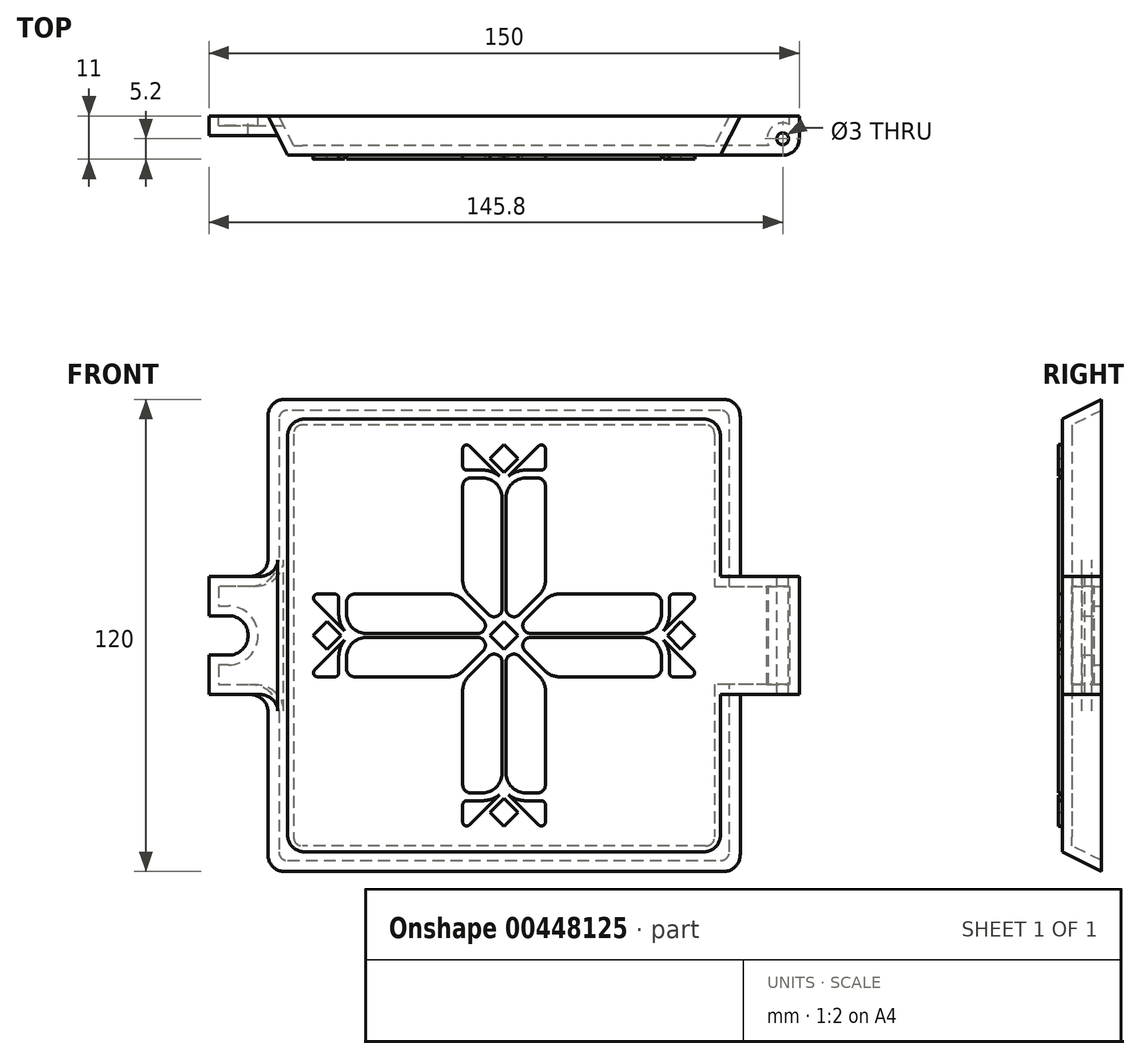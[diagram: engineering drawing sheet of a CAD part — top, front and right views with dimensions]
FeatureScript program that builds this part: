
annotation { "Feature Type Name" : "Feature", "Feature Type Description" : "" }
export const myFeature = defineFeature(function(context is Context, id is Id, definition is map)
    precondition{}
    {
        {
            var Q0;
            Q0=qCreatedBy(makeId("Front.planeOp"),FACE);
            var sketch = newSketch(context, id + "F0", { "sketchPlane" : qUnion([Q0])});
            skLineSegment(sketch, "E0.bottom", {"start": v(60, 60) * mm, "end": v(-60, 60) * mm});
            skLineSegment(sketch, "E0.top", {"start": v(60, -60) * mm, "end": v(-60, -60) * mm});
            skLineSegment(sketch, "E0.left", {"start": v(60, 60) * mm, "end": v(60, -60) * mm});
            skLineSegment(sketch, "E0.right", {"start": v(-60, 60) * mm, "end": v(-60, -60) * mm});
            skPoint(sketch, "E0.middle", {"position": v(0, 0) * mm});
            skLineSegment(sketch, "E1", {"start": v(60, 15) * mm, "end": v(75, 15) * mm});
            skLineSegment(sketch, "E2", {"start": v(75, 15) * mm, "end": v(75, -15) * mm});
            skLineSegment(sketch, "E3", {"start": v(75, -15) * mm, "end": v(60, -15) * mm});
            skLineSegment(sketch, "E4", {"start": v(-60, 15) * mm, "end": v(-75, 15) * mm});
            skLineSegment(sketch, "E5", {"start": v(-75, 15) * mm, "end": v(-75, 5) * mm});
            skLineSegment(sketch, "E6", {"start": v(-75, 5) * mm, "end": v(-70, 5) * mm});
            skLineSegment(sketch, "E7", {"start": v(-65, 0) * mm, "end": v(-65, 0) * mm});
            skLineSegment(sketch, "E8", {"start": v(-70, -5) * mm, "end": v(-75, -5) * mm});
            skLineSegment(sketch, "E9", {"start": v(-75, -5) * mm, "end": v(-75, -15) * mm});
            skLineSegment(sketch, "E10", {"start": v(-75, -15) * mm, "end": v(-60, -15) * mm});
            skPoint(sketch, "E11.visualSharp", {"position": v(-65, 5) * mm});
            skArc(sketch, "E11.filletArc", {"start": v(-65, 0) * mm, "mid": v(-66.46, 3.54) * mm, "end": v(-70, 5) * mm});
            skPoint(sketch, "E12.visualSharp", {"position": v(-65, -5) * mm});
            skArc(sketch, "E12.filletArc", {"start": v(-70, -5) * mm, "mid": v(-66.46, -3.54) * mm, "end": v(-65, 0) * mm});
            skSolve(sketch);
        }
        {
            var Q0;
            {var subQ3=sQuery(id+"F0.wireOp",EDGE,"E0.bottom");Q0=makeQuery(id+"F0.imprint","IMPRINT",FACE,{"disambiguationData":[TD([[makeQuery(id+"F0.imprint","IMPRINT",EDGE,{"derivedFrom":subQ3}),1.0]])]});}
            var Q1;
            {var subQ0=sQuery(id+"F0.wireOp",EDGE,"E1");Q1=makeQuery(id+"F0.imprint","IMPRINT",FACE,{"disambiguationData":[TD([[makeQuery(id+"F0.imprint","IMPRINT",EDGE,{"derivedFrom":subQ0}),-1.0]])]});}
            extrude(context, id + "F1", {"entities" : qUnion([Q0, Q1]), "depth" : 10 * mm});
        }
        {
            var Q0;
            {var subQ0=sQuery(id+"F0.wireOp",EDGE,"E4");Q0=makeQuery(id+"F0.imprint","IMPRINT",FACE,{"disambiguationData":[TD([[makeQuery(id+"F0.imprint","IMPRINT",EDGE,{"derivedFrom":subQ0}),1.0]])]});}
            extrude(context, id + "F2", {"entities" : qUnion([Q0]), "operationType" : NewBodyOperationType.ADD, "depth" : 5 * mm});
        }
        {
            var Q0;
            Q0=makeQuery(id+"F1.opExtrude","CAP_EDGE",EDGE,{"disambiguationData":[OSD([sQuery(id+"F0.wireOp",EDGE,"E0.bottom")])],"isStart":false});
            var Q1;
            {var subQ0=sQuery(id+"F0.wireOp",EDGE,"E0.left");Q1=makeQuery(id+"F1.opExtrude","CAP_EDGE",EDGE,{"disambiguationData":[OSD([subQ0]),TDD([makeQuery(id+"F0.imprint","IMPRINT",EDGE,{"disambiguationData":[TD([[makeQuery(id+"F0.imprint","INTERSECT",VERTEX,{"derivedFrom":[sQuery(id+"F0.wireOp",EDGE,"E0.bottom"),subQ0]}),-1.0]])],"derivedFrom":subQ0})])],"isStart":false});}
            var Q2;
            {var subQ0=sQuery(id+"F0.wireOp",EDGE,"E0.left");Q2=makeQuery(id+"F1.opExtrude","CAP_EDGE",EDGE,{"disambiguationData":[OSD([subQ0]),TDD([makeQuery(id+"F0.imprint","IMPRINT",EDGE,{"disambiguationData":[TD([[makeQuery(id+"F0.imprint","INTERSECT",VERTEX,{"derivedFrom":[sQuery(id+"F0.wireOp",EDGE,"E0.top"),subQ0]}),1.0]])],"derivedFrom":subQ0})])],"isStart":false});}
            var Q3;
            Q3=makeQuery(id+"F1.opExtrude","CAP_EDGE",EDGE,{"disambiguationData":[OSD([sQuery(id+"F0.wireOp",EDGE,"E0.top")])],"isStart":false});
            var Q4;
            Q4=makeQuery(id+"F1.opExtrude","CAP_EDGE",EDGE,{"disambiguationData":[OSD([sQuery(id+"F0.wireOp",EDGE,"E0.right")])],"isStart":false});
            chamfer(context, id + "F3", {"entities" : qUnion([Q0, Q1, Q2, Q3, Q4]), "chamferType" : ChamferType.TWO_OFFSETS, "width1" : 5 * mm, "oppositeDirection" : false, "width2" : 10 * mm, "tangentPropagation" : true});
        }
        {
            var Q0;
            Q0=makeQuery(id+"F1.opExtrude","CAP_EDGE",EDGE,{"disambiguationData":[OSD([sQuery(id+"F0.wireOp",EDGE,"E2")])],"isStart":false});
            var Q1;
            Q1=makeQuery(id+"F3.opChamfer","BLEND_EDGE",EDGE,{"blendedFrom":[makeQuery(id+"F1.opExtrude","CAP_EDGE",EDGE,{"disambiguationData":[OSD([sQuery(id+"F0.wireOp",EDGE,"E0.right")])],"isStart":false}),makeQuery(id+"F2.opExtrude","SWEPT_FACE",FACE,{"disambiguationData":[OSD([sQuery(id+"F0.wireOp",EDGE,"E4")])]})],"blendedInto":[makeQuery(id+"F2.opExtrude","SWEPT_FACE",FACE,{"disambiguationData":[OSD([sQuery(id+"F0.wireOp",EDGE,"E4")])]})]});
            var Q2;
            Q2=makeQuery(id+"F3.opChamfer","BLEND_EDGE",EDGE,{"blendedFrom":[makeQuery(id+"F1.opExtrude","CAP_EDGE",EDGE,{"disambiguationData":[OSD([sQuery(id+"F0.wireOp",EDGE,"E0.right")])],"isStart":false}),makeQuery(id+"F2.opExtrude","SWEPT_FACE",FACE,{"disambiguationData":[OSD([sQuery(id+"F0.wireOp",EDGE,"E10")])]})],"blendedInto":[makeQuery(id+"F2.opExtrude","SWEPT_FACE",FACE,{"disambiguationData":[OSD([sQuery(id+"F0.wireOp",EDGE,"E10")])]})]});
            fillet(context, id + "F4", {"entities" : qUnion([Q0, Q1, Q2]), "radius" : 4.2 * mm, "tangentPropagation" : true, "allowEdgeOverflow" : false});
        }
        {
            var Q0;
            Q0=makeQuery(id+"F1.opExtrude","SWEPT_FACE",FACE,{"disambiguationData":[OSD([sQuery(id+"F0.wireOp",EDGE,"E1")])]});
            var sketch = newSketch(context, id + "F5", { "sketchPlane" : qUnion([Q0])});
            skPoint(sketch, "E13", {"position": v(70.8, -5.8) * mm});
            skSolve(sketch);
        }
        {
            var Q0;
            Q0=sQuery(id+"F5.wireOp",VERTEX,"E13");
            var Q1;
            Q1=makeQuery(id+"F1.opExtrude","SWEPT_BODY",BODY,{"disambiguationData":[OSD([sQuery(id+"F0.wireOp",EDGE,"E0.bottom"),sQuery(id+"F0.wireOp",EDGE,"E0.top"),sQuery(id+"F0.wireOp",EDGE,"E0.left"),sQuery(id+"F0.wireOp",EDGE,"E0.right"),sQuery(id+"F0.wireOp",EDGE,"E1"),sQuery(id+"F0.wireOp",EDGE,"E2"),sQuery(id+"F0.wireOp",EDGE,"E3")])]});
            hole(context, id + "F6", {"style" : HoleStyle.SIMPLE, "endStyle" : HoleEndStyle.THROUGH, "holeDiameter" : 3 * mm, "isTappedThrough" : true, "tappedDepth" : 12 * mm, "tapClearance" : 3, "locations" : qUnion([Q0]), "scope" : qUnion([Q1])});
        }
        {
            var Q0;
            {var subQ0=sQuery(id+"F0.wireOp",EDGE,"E0.left");var subQ1=sQuery(id+"F0.wireOp",EDGE,"E0.bottom");Q0=makeQuery(id+"F3.opChamfer","BLEND_EDGE",EDGE,{"blendedFrom":[makeQuery(id+"F1.opExtrude","CAP_EDGE",EDGE,{"disambiguationData":[OSD([subQ1])],"isStart":false}),makeQuery(id+"F1.opExtrude","CAP_EDGE",EDGE,{"disambiguationData":[OSD([subQ0]),TDD([makeQuery(id+"F0.imprint","IMPRINT",EDGE,{"disambiguationData":[TD([[makeQuery(id+"F0.imprint","INTERSECT",VERTEX,{"derivedFrom":[subQ1,subQ0]}),-1.0]])],"derivedFrom":subQ0})])],"isStart":false})],"blendedInto":[]});}
            var Q1;
            {var subQ0=sQuery(id+"F0.wireOp",EDGE,"E0.left");var subQ1=sQuery(id+"F0.wireOp",EDGE,"E0.top");Q1=makeQuery(id+"F3.opChamfer","BLEND_EDGE",EDGE,{"blendedFrom":[makeQuery(id+"F1.opExtrude","CAP_EDGE",EDGE,{"disambiguationData":[OSD([subQ1])],"isStart":false}),makeQuery(id+"F1.opExtrude","CAP_EDGE",EDGE,{"disambiguationData":[OSD([subQ0]),TDD([makeQuery(id+"F0.imprint","IMPRINT",EDGE,{"disambiguationData":[TD([[makeQuery(id+"F0.imprint","INTERSECT",VERTEX,{"derivedFrom":[subQ1,subQ0]}),1.0]])],"derivedFrom":subQ0})])],"isStart":false})],"blendedInto":[]});}
            var Q2;
            Q2=makeQuery(id+"F3.opChamfer","BLEND_EDGE",EDGE,{"blendedFrom":[makeQuery(id+"F1.opExtrude","CAP_EDGE",EDGE,{"disambiguationData":[OSD([sQuery(id+"F0.wireOp",EDGE,"E0.bottom")])],"isStart":false}),makeQuery(id+"F1.opExtrude","CAP_EDGE",EDGE,{"disambiguationData":[OSD([sQuery(id+"F0.wireOp",EDGE,"E0.right")])],"isStart":false})],"blendedInto":[]});
            var Q3;
            Q3=makeQuery(id+"F3.opChamfer","BLEND_EDGE",EDGE,{"blendedFrom":[makeQuery(id+"F1.opExtrude","CAP_EDGE",EDGE,{"disambiguationData":[OSD([sQuery(id+"F0.wireOp",EDGE,"E0.top")])],"isStart":false}),makeQuery(id+"F1.opExtrude","CAP_EDGE",EDGE,{"disambiguationData":[OSD([sQuery(id+"F0.wireOp",EDGE,"E0.right")])],"isStart":false})],"blendedInto":[]});
            fillet(context, id + "F7", {"entities" : qUnion([Q0, Q1, Q2, Q3]), "radius" : 5 * mm, "tangentPropagation" : true, "allowEdgeOverflow" : false});
        }
        {
            var Q0;
            {var subQ0=sQuery(id+"F0.wireOp",EDGE,"E0.right");Q0=makeQuery(id+"F2.boolean.opBoolean","MERGE",FACE,{"derivedFrom":[makeQuery(id+"F1.opExtrude","CAP_FACE",FACE,{"disambiguationData":[OSD([sQuery(id+"F0.wireOp",EDGE,"E0.bottom"),sQuery(id+"F0.wireOp",EDGE,"E0.top"),sQuery(id+"F0.wireOp",EDGE,"E0.left"),subQ0,sQuery(id+"F0.wireOp",EDGE,"E1"),sQuery(id+"F0.wireOp",EDGE,"E2"),sQuery(id+"F0.wireOp",EDGE,"E3")])],"isStart":true}),makeQuery(id+"F2.opExtrude","CAP_FACE",FACE,{"disambiguationData":[OSD([subQ0,sQuery(id+"F0.wireOp",EDGE,"E4"),sQuery(id+"F0.wireOp",EDGE,"E5"),sQuery(id+"F0.wireOp",EDGE,"E6"),sQuery(id+"F0.wireOp",EDGE,"E8"),sQuery(id+"F0.wireOp",EDGE,"E9"),sQuery(id+"F0.wireOp",EDGE,"E10"),sQuery(id+"F0.wireOp",EDGE,"E11.filletArc"),sQuery(id+"F0.wireOp",EDGE,"E12.filletArc")])],"isStart":true})]});}
            shell(context, id + "F8", {"entities" : qUnion([Q0]), "thickness" : 2.5 * mm});
        }
        {
            var Q0;
            Q0=makeQuery(id+"F1.opExtrude","CAP_FACE",FACE,{"disambiguationData":[OSD([sQuery(id+"F0.wireOp",EDGE,"E0.bottom"),sQuery(id+"F0.wireOp",EDGE,"E0.top"),sQuery(id+"F0.wireOp",EDGE,"E0.left"),sQuery(id+"F0.wireOp",EDGE,"E0.right"),sQuery(id+"F0.wireOp",EDGE,"E1"),sQuery(id+"F0.wireOp",EDGE,"E2"),sQuery(id+"F0.wireOp",EDGE,"E3")])],"isStart":false});
            var sketch = newSketch(context, id + "F9", { "sketchPlane" : qUnion([Q0])});
            skLineSegment(sketch, "E14.bottom", {"start": v(55, 55) * mm, "end": v(-55, 55) * mm, "construction": true});
            skLineSegment(sketch, "E14.top", {"start": v(55, -55) * mm, "end": v(-55, -55) * mm, "construction": true});
            skLineSegment(sketch, "E14.left", {"start": v(55, 55) * mm, "end": v(55, -55) * mm, "construction": true});
            skLineSegment(sketch, "E14.right", {"start": v(-55, 55) * mm, "end": v(-55, -55) * mm, "construction": true});
            skPoint(sketch, "E14.middle", {"position": v(0, 0) * mm});
            skPoint(sketch, "E14.middle.positionSnap0", {"position": v(-55, 0) * mm});
            skPoint(sketch, "E14.middle.positionSnap1", {"position": v(0, 55) * mm});
            skPoint(sketch, "E14.centerSnap0", {"position": v(-55, 0) * mm});
            skPoint(sketch, "E14.centerSnap1", {"position": v(0, 55) * mm});
            skLineSegment(sketch, "E15", {"start": v(-55, 0) * mm, "end": v(55, 0) * mm, "construction": true});
            skLineSegment(sketch, "E16", {"start": v(0, 55) * mm, "end": v(0, -55) * mm, "construction": true});
            skLineSegment(sketch, "E17", {"start": v(-55, -55) * mm, "end": v(55, 55) * mm, "construction": true});
            skLineSegment(sketch, "E18", {"start": v(-55, 55) * mm, "end": v(55, -55) * mm, "construction": true});
            skLineSegment(sketch, "E19", {"start": v(0, 3.54) * mm, "end": v(3.54, 0) * mm});
            skLineSegment(sketch, "E20", {"start": v(3.54, 0) * mm, "end": v(0, -3.54) * mm});
            skLineSegment(sketch, "E21", {"start": v(0, -3.54) * mm, "end": v(-3.54, 0) * mm});
            skLineSegment(sketch, "E22", {"start": v(-3.54, 0) * mm, "end": v(0, 3.54) * mm});
            skLineSegment(sketch, "E23.1.0.0", {"start": v(45, 3.54) * mm, "end": v(48.54, 0) * mm});
            skLineSegment(sketch, "E23.1.0.1", {"start": v(48.54, 0) * mm, "end": v(45, -3.54) * mm});
            skLineSegment(sketch, "E23.1.0.2", {"start": v(45, -3.54) * mm, "end": v(41.46, 0) * mm});
            skLineSegment(sketch, "E23.1.0.3", {"start": v(41.46, 0) * mm, "end": v(45, 3.54) * mm});
            skLineSegment(sketch, "E23.direction1", {"start": v(3.54, 0) * mm, "end": v(48.54, 0) * mm, "construction": true});
            skLineSegment(sketch, "E24", {"start": v(5.33, 3.91) * mm, "end": v(10.45, 9.04) * mm});
            skLineSegment(sketch, "E25", {"start": v(6.74, 0.5) * mm, "end": v(35, 0.5) * mm});
            skLineSegment(sketch, "E26", {"start": v(39.33, 0) * mm, "end": v(48.12, 8.8) * mm});
            skLineSegment(sketch, "E27", {"start": v(38, 10.5) * mm, "end": v(13.99, 10.5) * mm});
            skLineSegment(sketch, "E28", {"start": v(40, 5.5) * mm, "end": v(40, 8.5) * mm});
            skPoint(sketch, "E29.visualSharp", {"position": v(1.91, 0.5) * mm});
            skArc(sketch, "E29.filletArc", {"start": v(5.33, 3.91) * mm, "mid": v(4.9, 1.73) * mm, "end": v(6.74, 0.5) * mm});
            skPoint(sketch, "E30.visualSharp", {"position": v(11.91, 10.5) * mm});
            skArc(sketch, "E30.filletArc", {"start": v(13.99, 10.5) * mm, "mid": v(12.07, 10.12) * mm, "end": v(10.45, 9.04) * mm});
            skArc(sketch, "E31.filletArc", {"start": v(35, 0.5) * mm, "mid": v(38.54, 1.96) * mm, "end": v(40, 5.5) * mm});
            skArc(sketch, "E32.filletArc", {"start": v(40, 8.5) * mm, "mid": v(39.41, 9.91) * mm, "end": v(38, 10.5) * mm});
            skArc(sketch, "E33.0", {"start": v(39.33, 0) * mm, "mid": v(41.3, 2.44) * mm, "end": v(42, 5.5) * mm});
            skLineSegment(sketch, "E34", {"start": v(42, 5.5) * mm, "end": v(42, 9.5) * mm});
            skLineSegment(sketch, "E35", {"start": v(43, 10.5) * mm, "end": v(47.42, 10.5) * mm});
            skPoint(sketch, "E36.visualSharp", {"position": v(42, 10.5) * mm});
            skArc(sketch, "E36.filletArc", {"start": v(43, 10.5) * mm, "mid": v(42.3, 10.2) * mm, "end": v(42, 9.5) * mm});
            skPoint(sketch, "E37.visualSharp", {"position": v(49.83, 10.5) * mm});
            skArc(sketch, "E37.filletArc", {"start": v(48.12, 8.8) * mm, "mid": v(48.34, 9.88) * mm, "end": v(47.42, 10.5) * mm});
            skLineSegment(sketch, "E38", {"start": v(41.46, 0) * mm, "end": v(48.54, 0) * mm});
            skLineSegment(sketch, "E39.MirrorCS", {"start": v(6.74, -0.5) * mm, "end": v(35, -0.5) * mm});
            skArc(sketch, "E40.MirrorCS", {"start": v(5.33, -3.91) * mm, "mid": v(4.9, -1.73) * mm, "end": v(6.74, -0.5) * mm});
            skLineSegment(sketch, "E41.MirrorCS", {"start": v(5.33, -3.91) * mm, "end": v(10.45, -9.04) * mm});
            skPoint(sketch, "E42.MirrorP", {"position": v(11.91, -10.5) * mm});
            skLineSegment(sketch, "E43.MirrorCS", {"start": v(38, -10.5) * mm, "end": v(13.99, -10.5) * mm});
            skArc(sketch, "E44.MirrorCS", {"start": v(13.99, -10.5) * mm, "mid": v(12.07, -10.12) * mm, "end": v(10.45, -9.04) * mm});
            skArc(sketch, "E45.MirrorCS", {"start": v(40, -8.5) * mm, "mid": v(39.41, -9.91) * mm, "end": v(38, -10.5) * mm});
            skLineSegment(sketch, "E46.MirrorCS", {"start": v(40, -5.5) * mm, "end": v(40, -8.5) * mm});
            skArc(sketch, "E47.MirrorCS", {"start": v(35, -0.5) * mm, "mid": v(38.54, -1.96) * mm, "end": v(40, -5.5) * mm});
            skLineSegment(sketch, "E48.MirrorCS", {"start": v(39.33, 0) * mm, "end": v(48.12, -8.8) * mm});
            skLineSegment(sketch, "E49.MirrorCS", {"start": v(43, -10.5) * mm, "end": v(47.42, -10.5) * mm});
            skArc(sketch, "E50.MirrorCS", {"start": v(48.12, -8.8) * mm, "mid": v(48.34, -9.88) * mm, "end": v(47.42, -10.5) * mm});
            skArc(sketch, "E51.MirrorCS", {"start": v(43, -10.5) * mm, "mid": v(42.3, -10.2) * mm, "end": v(42, -9.5) * mm});
            skLineSegment(sketch, "E52.MirrorCS", {"start": v(42, -5.5) * mm, "end": v(42, -9.5) * mm});
            skArc(sketch, "E53.MirrorCS", {"start": v(39.33, 0) * mm, "mid": v(41.3, -2.44) * mm, "end": v(42, -5.5) * mm});
            skLineSegment(sketch, "E54.1.0", {"start": v(-0.5, -6.74) * mm, "end": v(-0.5, -35) * mm});
            skArc(sketch, "E54.1.1", {"start": v(-0.5, -35) * mm, "mid": v(-1.96, -38.54) * mm, "end": v(-5.5, -40) * mm});
            skLineSegment(sketch, "E54.1.2", {"start": v(-3.54, -45) * mm, "end": v(0, -41.46) * mm});
            skLineSegment(sketch, "E54.1.3", {"start": v(0, -41.46) * mm, "end": v(3.54, -45) * mm});
            skArc(sketch, "E54.1.5", {"start": v(3.91, -5.33) * mm, "mid": v(1.73, -4.9) * mm, "end": v(0.5, -6.74) * mm});
            skLineSegment(sketch, "E54.1.6", {"start": v(-5.5, -42) * mm, "end": v(-9.5, -42) * mm});
            skLineSegment(sketch, "E54.1.7", {"start": v(5.5, -42) * mm, "end": v(9.5, -42) * mm});
            skPoint(sketch, "E54.1.8", {"position": v(10.5, -42) * mm});
            skLineSegment(sketch, "E54.1.9", {"start": v(10.5, -38) * mm, "end": v(10.5, -13.99) * mm});
            skArc(sketch, "E54.1.10", {"start": v(0, -39.33) * mm, "mid": v(-2.44, -41.3) * mm, "end": v(-5.5, -42) * mm});
            skPoint(sketch, "E54.1.11", {"position": v(-10.5, -11.91) * mm});
            skLineSegment(sketch, "E54.1.12", {"start": v(3.91, -5.33) * mm, "end": v(9.04, -10.45) * mm});
            skLineSegment(sketch, "E54.1.13", {"start": v(3.54, -45) * mm, "end": v(0, -48.54) * mm});
            skLineSegment(sketch, "E54.1.14", {"start": v(0, -39.33) * mm, "end": v(8.8, -48.12) * mm});
            skLineSegment(sketch, "E54.1.15", {"start": v(-3.91, -5.33) * mm, "end": v(-9.04, -10.45) * mm});
            skPoint(sketch, "E54.1.16", {"position": v(10.5, -11.91) * mm});
            skLineSegment(sketch, "E54.1.17", {"start": v(0.5, -6.74) * mm, "end": v(0.5, -35) * mm});
            skArc(sketch, "E54.1.18", {"start": v(0.5, -35) * mm, "mid": v(1.96, -38.54) * mm, "end": v(5.5, -40) * mm});
            skLineSegment(sketch, "E54.1.19", {"start": v(0, -48.54) * mm, "end": v(-3.54, -45) * mm});
            skLineSegment(sketch, "E54.1.20", {"start": v(0, -39.33) * mm, "end": v(-8.8, -48.12) * mm});
            skArc(sketch, "E54.1.21", {"start": v(0, -39.33) * mm, "mid": v(2.44, -41.3) * mm, "end": v(5.5, -42) * mm});
            skLineSegment(sketch, "E54.1.22", {"start": v(-10.5, -38) * mm, "end": v(-10.5, -13.99) * mm});
            skArc(sketch, "E54.1.23", {"start": v(-3.91, -5.33) * mm, "mid": v(-1.73, -4.9) * mm, "end": v(-0.5, -6.74) * mm});
            skPoint(sketch, "E54.1.24", {"position": v(10.5, -49.83) * mm});
            skLineSegment(sketch, "E54.1.25", {"start": v(-10.5, -43) * mm, "end": v(-10.5, -47.42) * mm});
            skLineSegment(sketch, "E54.1.26", {"start": v(10.5, -43) * mm, "end": v(10.5, -47.42) * mm});
            skLineSegment(sketch, "E54.1.27", {"start": v(0, -41.46) * mm, "end": v(0, -48.54) * mm});
            skArc(sketch, "E54.1.28", {"start": v(10.5, -13.99) * mm, "mid": v(10.12, -12.07) * mm, "end": v(9.04, -10.45) * mm});
            skArc(sketch, "E54.1.29", {"start": v(-10.5, -13.99) * mm, "mid": v(-10.12, -12.07) * mm, "end": v(-9.04, -10.45) * mm});
            skLineSegment(sketch, "E54.1.30", {"start": v(5.5, -40) * mm, "end": v(8.5, -40) * mm});
            skLineSegment(sketch, "E54.1.31", {"start": v(-5.5, -40) * mm, "end": v(-8.5, -40) * mm});
            skArc(sketch, "E54.1.32", {"start": v(8.8, -48.12) * mm, "mid": v(9.88, -48.34) * mm, "end": v(10.5, -47.42) * mm});
            skArc(sketch, "E54.1.33", {"start": v(-8.5, -40) * mm, "mid": v(-9.91, -39.41) * mm, "end": v(-10.5, -38) * mm});
            skArc(sketch, "E54.1.34", {"start": v(10.5, -43) * mm, "mid": v(10.2, -42.3) * mm, "end": v(9.5, -42) * mm});
            skArc(sketch, "E54.1.35", {"start": v(-10.5, -43) * mm, "mid": v(-10.2, -42.3) * mm, "end": v(-9.5, -42) * mm});
            skArc(sketch, "E54.1.36", {"start": v(-8.8, -48.12) * mm, "mid": v(-9.88, -48.34) * mm, "end": v(-10.5, -47.42) * mm});
            skArc(sketch, "E54.1.37", {"start": v(8.5, -40) * mm, "mid": v(9.91, -39.41) * mm, "end": v(10.5, -38) * mm});
            skLineSegment(sketch, "E54.2.0", {"start": v(-6.74, 0.5) * mm, "end": v(-35, 0.5) * mm});
            skArc(sketch, "E54.2.1", {"start": v(-35, 0.5) * mm, "mid": v(-38.54, 1.96) * mm, "end": v(-40, 5.5) * mm});
            skLineSegment(sketch, "E54.2.2", {"start": v(-45, 3.54) * mm, "end": v(-41.46, 0) * mm});
            skLineSegment(sketch, "E54.2.3", {"start": v(-41.46, 0) * mm, "end": v(-45, -3.54) * mm});
            skArc(sketch, "E54.2.5", {"start": v(-5.33, -3.91) * mm, "mid": v(-4.9, -1.73) * mm, "end": v(-6.74, -0.5) * mm});
            skLineSegment(sketch, "E54.2.6", {"start": v(-42, 5.5) * mm, "end": v(-42, 9.5) * mm});
            skLineSegment(sketch, "E54.2.7", {"start": v(-42, -5.5) * mm, "end": v(-42, -9.5) * mm});
            skPoint(sketch, "E54.2.8", {"position": v(-42, -10.5) * mm});
            skLineSegment(sketch, "E54.2.9", {"start": v(-38, -10.5) * mm, "end": v(-13.99, -10.5) * mm});
            skArc(sketch, "E54.2.10", {"start": v(-39.33, 0) * mm, "mid": v(-41.3, 2.44) * mm, "end": v(-42, 5.5) * mm});
            skPoint(sketch, "E54.2.11", {"position": v(-11.91, 10.5) * mm});
            skLineSegment(sketch, "E54.2.12", {"start": v(-5.33, -3.91) * mm, "end": v(-10.45, -9.04) * mm});
            skLineSegment(sketch, "E54.2.13", {"start": v(-45, -3.54) * mm, "end": v(-48.54, 0) * mm});
            skLineSegment(sketch, "E54.2.14", {"start": v(-39.33, 0) * mm, "end": v(-48.12, -8.8) * mm});
            skLineSegment(sketch, "E54.2.15", {"start": v(-5.33, 3.91) * mm, "end": v(-10.45, 9.04) * mm});
            skPoint(sketch, "E54.2.16", {"position": v(-11.91, -10.5) * mm});
            skLineSegment(sketch, "E54.2.17", {"start": v(-6.74, -0.5) * mm, "end": v(-35, -0.5) * mm});
            skArc(sketch, "E54.2.18", {"start": v(-35, -0.5) * mm, "mid": v(-38.54, -1.96) * mm, "end": v(-40, -5.5) * mm});
            skLineSegment(sketch, "E54.2.19", {"start": v(-48.54, 0) * mm, "end": v(-45, 3.54) * mm});
            skLineSegment(sketch, "E54.2.20", {"start": v(-39.33, 0) * mm, "end": v(-48.12, 8.8) * mm});
            skArc(sketch, "E54.2.21", {"start": v(-39.33, 0) * mm, "mid": v(-41.3, -2.44) * mm, "end": v(-42, -5.5) * mm});
            skLineSegment(sketch, "E54.2.22", {"start": v(-38, 10.5) * mm, "end": v(-13.99, 10.5) * mm});
            skArc(sketch, "E54.2.23", {"start": v(-5.33, 3.91) * mm, "mid": v(-4.9, 1.73) * mm, "end": v(-6.74, 0.5) * mm});
            skPoint(sketch, "E54.2.24", {"position": v(-49.83, -10.5) * mm});
            skLineSegment(sketch, "E54.2.25", {"start": v(-43, 10.5) * mm, "end": v(-47.42, 10.5) * mm});
            skLineSegment(sketch, "E54.2.26", {"start": v(-43, -10.5) * mm, "end": v(-47.42, -10.5) * mm});
            skLineSegment(sketch, "E54.2.27", {"start": v(-41.46, 0) * mm, "end": v(-48.54, 0) * mm});
            skArc(sketch, "E54.2.28", {"start": v(-13.99, -10.5) * mm, "mid": v(-12.07, -10.12) * mm, "end": v(-10.45, -9.04) * mm});
            skArc(sketch, "E54.2.29", {"start": v(-13.99, 10.5) * mm, "mid": v(-12.07, 10.12) * mm, "end": v(-10.45, 9.04) * mm});
            skLineSegment(sketch, "E54.2.30", {"start": v(-40, -5.5) * mm, "end": v(-40, -8.5) * mm});
            skLineSegment(sketch, "E54.2.31", {"start": v(-40, 5.5) * mm, "end": v(-40, 8.5) * mm});
            skArc(sketch, "E54.2.32", {"start": v(-48.12, -8.8) * mm, "mid": v(-48.34, -9.88) * mm, "end": v(-47.42, -10.5) * mm});
            skArc(sketch, "E54.2.33", {"start": v(-40, 8.5) * mm, "mid": v(-39.41, 9.91) * mm, "end": v(-38, 10.5) * mm});
            skArc(sketch, "E54.2.34", {"start": v(-43, -10.5) * mm, "mid": v(-42.3, -10.2) * mm, "end": v(-42, -9.5) * mm});
            skArc(sketch, "E54.2.35", {"start": v(-43, 10.5) * mm, "mid": v(-42.3, 10.2) * mm, "end": v(-42, 9.5) * mm});
            skArc(sketch, "E54.2.36", {"start": v(-48.12, 8.8) * mm, "mid": v(-48.34, 9.88) * mm, "end": v(-47.42, 10.5) * mm});
            skArc(sketch, "E54.2.37", {"start": v(-40, -8.5) * mm, "mid": v(-39.41, -9.91) * mm, "end": v(-38, -10.5) * mm});
            skLineSegment(sketch, "E54.3.0", {"start": v(0.5, 6.74) * mm, "end": v(0.5, 35) * mm});
            skArc(sketch, "E54.3.1", {"start": v(0.5, 35) * mm, "mid": v(1.96, 38.54) * mm, "end": v(5.5, 40) * mm});
            skLineSegment(sketch, "E54.3.2", {"start": v(3.54, 45) * mm, "end": v(0, 41.46) * mm});
            skLineSegment(sketch, "E54.3.3", {"start": v(0, 41.46) * mm, "end": v(-3.54, 45) * mm});
            skArc(sketch, "E54.3.5", {"start": v(-3.91, 5.33) * mm, "mid": v(-1.73, 4.9) * mm, "end": v(-0.5, 6.74) * mm});
            skLineSegment(sketch, "E54.3.6", {"start": v(5.5, 42) * mm, "end": v(9.5, 42) * mm});
            skLineSegment(sketch, "E54.3.7", {"start": v(-5.5, 42) * mm, "end": v(-9.5, 42) * mm});
            skPoint(sketch, "E54.3.8", {"position": v(-10.5, 42) * mm});
            skLineSegment(sketch, "E54.3.9", {"start": v(-10.5, 38) * mm, "end": v(-10.5, 13.99) * mm});
            skArc(sketch, "E54.3.10", {"start": v(0, 39.33) * mm, "mid": v(2.44, 41.3) * mm, "end": v(5.5, 42) * mm});
            skPoint(sketch, "E54.3.11", {"position": v(10.5, 11.91) * mm});
            skLineSegment(sketch, "E54.3.12", {"start": v(-3.91, 5.33) * mm, "end": v(-9.04, 10.45) * mm});
            skLineSegment(sketch, "E54.3.13", {"start": v(-3.54, 45) * mm, "end": v(0, 48.54) * mm});
            skLineSegment(sketch, "E54.3.14", {"start": v(0, 39.33) * mm, "end": v(-8.8, 48.12) * mm});
            skLineSegment(sketch, "E54.3.15", {"start": v(3.91, 5.33) * mm, "end": v(9.04, 10.45) * mm});
            skPoint(sketch, "E54.3.16", {"position": v(-10.5, 11.91) * mm});
            skLineSegment(sketch, "E54.3.17", {"start": v(-0.5, 6.74) * mm, "end": v(-0.5, 35) * mm});
            skArc(sketch, "E54.3.18", {"start": v(-0.5, 35) * mm, "mid": v(-1.96, 38.54) * mm, "end": v(-5.5, 40) * mm});
            skLineSegment(sketch, "E54.3.19", {"start": v(0, 48.54) * mm, "end": v(3.54, 45) * mm});
            skLineSegment(sketch, "E54.3.20", {"start": v(0, 39.33) * mm, "end": v(8.8, 48.12) * mm});
            skArc(sketch, "E54.3.21", {"start": v(0, 39.33) * mm, "mid": v(-2.44, 41.3) * mm, "end": v(-5.5, 42) * mm});
            skLineSegment(sketch, "E54.3.22", {"start": v(10.5, 38) * mm, "end": v(10.5, 13.99) * mm});
            skArc(sketch, "E54.3.23", {"start": v(3.91, 5.33) * mm, "mid": v(1.73, 4.9) * mm, "end": v(0.5, 6.74) * mm});
            skPoint(sketch, "E54.3.24", {"position": v(-10.5, 49.83) * mm});
            skLineSegment(sketch, "E54.3.25", {"start": v(10.5, 43) * mm, "end": v(10.5, 47.42) * mm});
            skLineSegment(sketch, "E54.3.26", {"start": v(-10.5, 43) * mm, "end": v(-10.5, 47.42) * mm});
            skLineSegment(sketch, "E54.3.27", {"start": v(0, 41.46) * mm, "end": v(0, 48.54) * mm});
            skArc(sketch, "E54.3.28", {"start": v(-10.5, 13.99) * mm, "mid": v(-10.12, 12.07) * mm, "end": v(-9.04, 10.45) * mm});
            skArc(sketch, "E54.3.29", {"start": v(10.5, 13.99) * mm, "mid": v(10.12, 12.07) * mm, "end": v(9.04, 10.45) * mm});
            skLineSegment(sketch, "E54.3.30", {"start": v(-5.5, 40) * mm, "end": v(-8.5, 40) * mm});
            skLineSegment(sketch, "E54.3.31", {"start": v(5.5, 40) * mm, "end": v(8.5, 40) * mm});
            skArc(sketch, "E54.3.32", {"start": v(-8.8, 48.12) * mm, "mid": v(-9.88, 48.34) * mm, "end": v(-10.5, 47.42) * mm});
            skArc(sketch, "E54.3.33", {"start": v(8.5, 40) * mm, "mid": v(9.91, 39.41) * mm, "end": v(10.5, 38) * mm});
            skArc(sketch, "E54.3.34", {"start": v(-10.5, 43) * mm, "mid": v(-10.2, 42.3) * mm, "end": v(-9.5, 42) * mm});
            skArc(sketch, "E54.3.35", {"start": v(10.5, 43) * mm, "mid": v(10.2, 42.3) * mm, "end": v(9.5, 42) * mm});
            skArc(sketch, "E54.3.36", {"start": v(8.8, 48.12) * mm, "mid": v(9.88, 48.34) * mm, "end": v(10.5, 47.42) * mm});
            skArc(sketch, "E54.3.37", {"start": v(-8.5, 40) * mm, "mid": v(-9.91, 39.41) * mm, "end": v(-10.5, 38) * mm});
            skLineSegment(sketch, "E54.anchor1", {"start": v(0, 0) * mm, "end": v(13.99, -5.5) * mm, "construction": true});
            skLineSegment(sketch, "E54.anchor2", {"start": v(0, 0) * mm, "end": v(5.5, 13.99) * mm, "construction": true});
            skSolve(sketch);
        }
        {
            var Q0;
            Q0=makeQuery(id+"F9.imprint","IMPRINT",FACE,{"disambiguationData":[TD([[makeQuery(id+"F9.imprint","IMPRINT",EDGE,{"derivedFrom":sQuery(id+"F9.wireOp",EDGE,"E19")}),-1.0]])]});
            var Q1;
            Q1=makeQuery(id+"F9.imprint","IMPRINT",FACE,{"disambiguationData":[TD([[makeQuery(id+"F9.imprint","IMPRINT",EDGE,{"derivedFrom":sQuery(id+"F9.wireOp",EDGE,"E24")}),-1.0]])]});
            var Q2;
            {var subQ0=sQuery(id+"F9.wireOp",EDGE,"E34");Q2=makeQuery(id+"F9.imprint","IMPRINT",FACE,{"disambiguationData":[TD([[makeQuery(id+"F9.imprint","IMPRINT",EDGE,{"derivedFrom":subQ0}),-1.0]])]});}
            var Q3;
            Q3=makeQuery(id+"F9.imprint","IMPRINT",FACE,{"disambiguationData":[TD([[makeQuery(id+"F9.imprint","IMPRINT",EDGE,{"derivedFrom":sQuery(id+"F9.wireOp",EDGE,"E23.1.0.0")}),-1.0]])]});
            var Q4;
            Q4=makeQuery(id+"F9.imprint","IMPRINT",FACE,{"disambiguationData":[TD([[makeQuery(id+"F9.imprint","IMPRINT",EDGE,{"derivedFrom":sQuery(id+"F9.wireOp",EDGE,"E23.1.0.1")}),-1.0]])]});
            var Q5;
            Q5=makeQuery(id+"F9.imprint","IMPRINT",FACE,{"disambiguationData":[TD([[makeQuery(id+"F9.imprint","IMPRINT",EDGE,{"derivedFrom":sQuery(id+"F9.wireOp",EDGE,"E49.MirrorCS")}),1.0]])]});
            var Q6;
            Q6=makeQuery(id+"F9.imprint","IMPRINT",FACE,{"disambiguationData":[TD([[makeQuery(id+"F9.imprint","IMPRINT",EDGE,{"derivedFrom":sQuery(id+"F9.wireOp",EDGE,"E39.MirrorCS")}),-1.0]])]});
            var Q7;
            Q7=makeQuery(id+"F9.imprint","IMPRINT",FACE,{"disambiguationData":[TD([[makeQuery(id+"F9.imprint","IMPRINT",EDGE,{"derivedFrom":sQuery(id+"F9.wireOp",EDGE,"E54.1.5")}),1.0]])]});
            var Q8;
            Q8=makeQuery(id+"F9.imprint","IMPRINT",FACE,{"disambiguationData":[TD([[makeQuery(id+"F9.imprint","IMPRINT",EDGE,{"derivedFrom":sQuery(id+"F9.wireOp",EDGE,"E54.1.0")}),-1.0]])]});
            var Q9;
            Q9=makeQuery(id+"F9.imprint","IMPRINT",FACE,{"disambiguationData":[TD([[makeQuery(id+"F9.imprint","IMPRINT",EDGE,{"derivedFrom":sQuery(id+"F9.wireOp",EDGE,"E54.2.5")}),1.0]])]});
            var Q10;
            Q10=makeQuery(id+"F9.imprint","IMPRINT",FACE,{"disambiguationData":[TD([[makeQuery(id+"F9.imprint","IMPRINT",EDGE,{"derivedFrom":sQuery(id+"F9.wireOp",EDGE,"E54.2.0")}),-1.0]])]});
            var Q11;
            Q11=makeQuery(id+"F9.imprint","IMPRINT",FACE,{"disambiguationData":[TD([[makeQuery(id+"F9.imprint","IMPRINT",EDGE,{"derivedFrom":sQuery(id+"F9.wireOp",EDGE,"E54.3.5")}),1.0]])]});
            var Q12;
            Q12=makeQuery(id+"F9.imprint","IMPRINT",FACE,{"disambiguationData":[TD([[makeQuery(id+"F9.imprint","IMPRINT",EDGE,{"derivedFrom":sQuery(id+"F9.wireOp",EDGE,"E54.3.0")}),-1.0]])]});
            var Q13;
            Q13=makeQuery(id+"F9.imprint","IMPRINT",FACE,{"disambiguationData":[TD([[makeQuery(id+"F9.imprint","IMPRINT",EDGE,{"derivedFrom":sQuery(id+"F9.wireOp",EDGE,"E54.2.3")}),-1.0]])]});
            var Q14;
            Q14=makeQuery(id+"F9.imprint","IMPRINT",FACE,{"disambiguationData":[TD([[makeQuery(id+"F9.imprint","IMPRINT",EDGE,{"derivedFrom":sQuery(id+"F9.wireOp",EDGE,"E54.2.2")}),-1.0]])]});
            var Q15;
            {var subQ4=sQuery(id+"F9.wireOp",EDGE,"E54.2.6");Q15=makeQuery(id+"F9.imprint","IMPRINT",FACE,{"disambiguationData":[TD([[makeQuery(id+"F9.imprint","IMPRINT",EDGE,{"derivedFrom":subQ4}),1.0]])]});}
            var Q16;
            {var subQ4=sQuery(id+"F9.wireOp",EDGE,"E54.2.7");Q16=makeQuery(id+"F9.imprint","IMPRINT",FACE,{"disambiguationData":[TD([[makeQuery(id+"F9.imprint","IMPRINT",EDGE,{"derivedFrom":subQ4}),-1.0]])]});}
            var Q17;
            {var subQ4=sQuery(id+"F9.wireOp",EDGE,"E54.1.7");Q17=makeQuery(id+"F9.imprint","IMPRINT",FACE,{"disambiguationData":[TD([[makeQuery(id+"F9.imprint","IMPRINT",EDGE,{"derivedFrom":subQ4}),-1.0]])]});}
            var Q18;
            Q18=makeQuery(id+"F9.imprint","IMPRINT",FACE,{"disambiguationData":[TD([[makeQuery(id+"F9.imprint","IMPRINT",EDGE,{"derivedFrom":sQuery(id+"F9.wireOp",EDGE,"E54.1.3")}),-1.0]])]});
            var Q19;
            Q19=makeQuery(id+"F9.imprint","IMPRINT",FACE,{"disambiguationData":[TD([[makeQuery(id+"F9.imprint","IMPRINT",EDGE,{"derivedFrom":sQuery(id+"F9.wireOp",EDGE,"E54.1.2")}),-1.0]])]});
            var Q20;
            {var subQ4=sQuery(id+"F9.wireOp",EDGE,"E54.1.6");Q20=makeQuery(id+"F9.imprint","IMPRINT",FACE,{"disambiguationData":[TD([[makeQuery(id+"F9.imprint","IMPRINT",EDGE,{"derivedFrom":subQ4}),1.0]])]});}
            var Q21;
            {var subQ4=sQuery(id+"F9.wireOp",EDGE,"E54.3.6");Q21=makeQuery(id+"F9.imprint","IMPRINT",FACE,{"disambiguationData":[TD([[makeQuery(id+"F9.imprint","IMPRINT",EDGE,{"derivedFrom":subQ4}),1.0]])]});}
            var Q22;
            {var subQ4=sQuery(id+"F9.wireOp",EDGE,"E54.3.7");Q22=makeQuery(id+"F9.imprint","IMPRINT",FACE,{"disambiguationData":[TD([[makeQuery(id+"F9.imprint","IMPRINT",EDGE,{"derivedFrom":subQ4}),-1.0]])]});}
            var Q23;
            Q23=makeQuery(id+"F9.imprint","IMPRINT",FACE,{"disambiguationData":[TD([[makeQuery(id+"F9.imprint","IMPRINT",EDGE,{"derivedFrom":sQuery(id+"F9.wireOp",EDGE,"E54.3.3")}),-1.0]])]});
            var Q24;
            Q24=makeQuery(id+"F9.imprint","IMPRINT",FACE,{"disambiguationData":[TD([[makeQuery(id+"F9.imprint","IMPRINT",EDGE,{"derivedFrom":sQuery(id+"F9.wireOp",EDGE,"E54.3.2")}),-1.0]])]});
            extrude(context, id + "F10", {"entities" : qUnion([Q0, Q1, Q2, Q3, Q4, Q5, Q6, Q7, Q8, Q9, Q10, Q11, Q12, Q13, Q14, Q15, Q16, Q17, Q18, Q19, Q20, Q21, Q22, Q23, Q24]), "operationType" : NewBodyOperationType.ADD, "depth" : 1 * mm});
        }
    });
